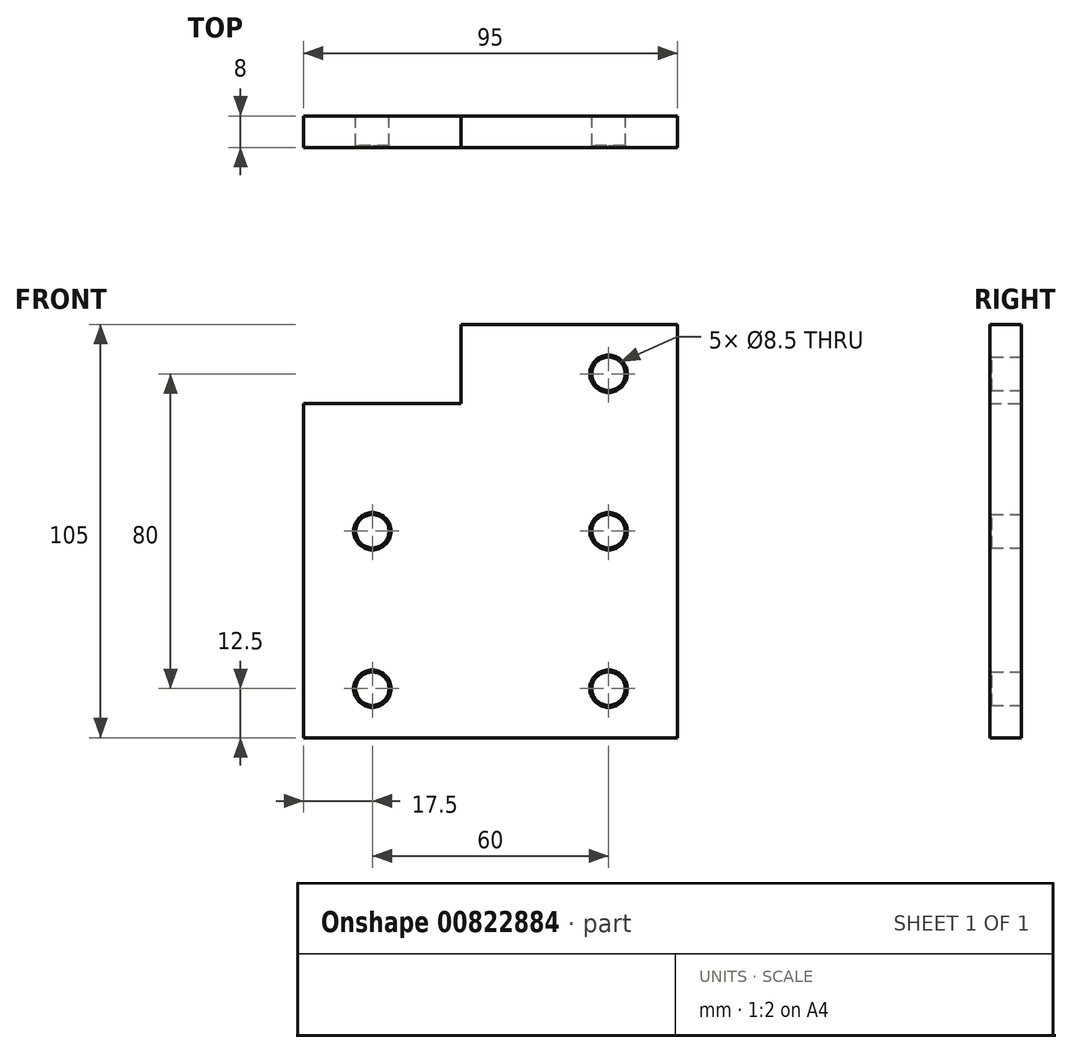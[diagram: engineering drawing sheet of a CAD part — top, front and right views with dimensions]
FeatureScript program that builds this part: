
annotation { "Feature Type Name" : "Feature", "Feature Type Description" : "" }
export const myFeature = defineFeature(function(context is Context, id is Id, definition is map)
    precondition{}
    {
        {
            var Q0;
            Q0=qCreatedBy(makeId("Front.planeOp"),FACE);
            var sketch = newSketch(context, id + "F0", { "sketchPlane" : qUnion([Q0])});
            skLineSegment(sketch, "E0.bottom", {"start": v(50, -52.5) * mm, "end": v(-45, -52.5) * mm});
            skLineSegment(sketch, "E0.top", {"start": v(50, 52.5) * mm, "end": v(-45, 52.5) * mm});
            skLineSegment(sketch, "E0.left", {"start": v(50, -52.5) * mm, "end": v(50, 52.5) * mm});
            skLineSegment(sketch, "E0.right", {"start": v(-45, -52.5) * mm, "end": v(-45, 52.5) * mm});
            skLineSegment(sketch, "E1", {"start": v(2.5, 0) * mm, "end": v(0, 0) * mm, "construction": true});
            skLineSegment(sketch, "E2.bottom", {"start": v(-27.5, 40) * mm, "end": v(32.5, 40) * mm, "construction": true});
            skLineSegment(sketch, "E2.top", {"start": v(-27.5, -40) * mm, "end": v(32.5, -40) * mm, "construction": true});
            skLineSegment(sketch, "E2.left", {"start": v(-27.5, 40) * mm, "end": v(-27.5, -40) * mm, "construction": true});
            skLineSegment(sketch, "E2.right", {"start": v(32.5, 40) * mm, "end": v(32.5, -40) * mm, "construction": true});
            skPoint(sketch, "E2.middle", {"position": v(2.5, 0) * mm});
            skCircle(sketch, "E3", {"center": v(-27.5, 40) * mm, "radius": 4.25 * mm, "construction": true});
            skCircle(sketch, "E4", {"center": v(32.5, 40) * mm, "radius": 4.25 * mm});
            skCircle(sketch, "E5", {"center": v(32.5, -40) * mm, "radius": 4.25 * mm});
            skCircle(sketch, "E6", {"center": v(-27.5, -40) * mm, "radius": 4.25 * mm});
            skCircle(sketch, "E7", {"center": v(-27.5, -40) * mm, "radius": 9 * mm, "construction": true});
            skLineSegment(sketch, "E8", {"start": v(-27.5, 0) * mm, "end": v(32.5, 0) * mm, "construction": true});
            skCircle(sketch, "E9", {"center": v(-27.5, 0) * mm, "radius": 4.25 * mm});
            skCircle(sketch, "E10", {"center": v(32.5, 0) * mm, "radius": 4.25 * mm});
            skSolve(sketch);
        }
        {
            var Q0;
            Q0=qSketchRegion(id+"F0",true);
            extrude(context, id + "F1", {"entities" : qUnion([Q0]), "depth" : 8 * mm, "offsetDistance" : 25 * mm});
        }
        {
            var Q0;
            Q0=makeQuery(id+"F1.opExtrude","CAP_EDGE",EDGE,{"disambiguationData":[OSD([sQuery(id+"F0.wireOp",EDGE,"E3")])],"isStart":false});
            var Q1;
            Q1=makeQuery(id+"F1.opExtrude","CAP_EDGE",EDGE,{"disambiguationData":[OSD([sQuery(id+"F0.wireOp",EDGE,"E4")])],"isStart":false});
            var Q2;
            Q2=makeQuery(id+"F1.opExtrude","CAP_EDGE",EDGE,{"disambiguationData":[OSD([sQuery(id+"F0.wireOp",EDGE,"E5")])],"isStart":false});
            var Q3;
            Q3=makeQuery(id+"F1.opExtrude","CAP_EDGE",EDGE,{"disambiguationData":[OSD([sQuery(id+"F0.wireOp",EDGE,"E6")])],"isStart":false});
            var Q4;
            Q4=makeQuery(id+"F1.opExtrude","CAP_EDGE",EDGE,{"disambiguationData":[OSD([sQuery(id+"F0.wireOp",EDGE,"E9")])],"isStart":false});
            var Q5;
            Q5=makeQuery(id+"F1.opExtrude","CAP_EDGE",EDGE,{"disambiguationData":[OSD([sQuery(id+"F0.wireOp",EDGE,"E10")])],"isStart":false});
            chamfer(context, id + "F2", {"entities" : qUnion([Q0, Q1, Q2, Q3, Q4, Q5]), "width" : 0.5 * mm, "tangentPropagation" : true});
        }
        {
            var Q0;
            Q0=makeQuery(id+"F1.opExtrude","CAP_FACE",FACE,{"disambiguationData":[OSD([sQuery(id+"F0.wireOp",EDGE,"E0.bottom"),sQuery(id+"F0.wireOp",EDGE,"E0.top"),sQuery(id+"F0.wireOp",EDGE,"E0.left"),sQuery(id+"F0.wireOp",EDGE,"E0.right"),sQuery(id+"F0.wireOp",EDGE,"E4"),sQuery(id+"F0.wireOp",EDGE,"E5"),sQuery(id+"F0.wireOp",EDGE,"E6"),sQuery(id+"F0.wireOp",EDGE,"E9"),sQuery(id+"F0.wireOp",EDGE,"E10")])],"isStart":false});
            var sketch = newSketch(context, id + "F3", { "sketchPlane" : qUnion([Q0])});
            skLineSegment(sketch, "E11.0", {"start": v(50, 52.5) * mm, "end": v(-45, 52.5) * mm, "construction": true});
            skLineSegment(sketch, "E12.0", {"start": v(-45, -52.5) * mm, "end": v(-45, 52.5) * mm, "construction": true});
            skLineSegment(sketch, "E13", {"start": v(-47.5, -14.2) * mm, "end": v(-47.5, 76.2) * mm, "construction": true});
            skLineSegment(sketch, "E14", {"start": v(-47.5, 76.2) * mm, "end": v(22.85, 76.2) * mm, "construction": true});
            skCircle(sketch, "E15", {"center": v(-17.5, 50.2) * mm, "radius": 12.5 * mm, "construction": true});
            skCircle(sketch, "E16", {"center": v(-17.5, 50.2) * mm, "radius": 10 * mm, "construction": true});
            skLineSegment(sketch, "E17", {"start": v(-5, 32.5) * mm, "end": v(-55, 32.5) * mm});
            skLineSegment(sketch, "E18", {"start": v(-55, 32.5) * mm, "end": v(-55, 88.36) * mm});
            skLineSegment(sketch, "E19", {"start": v(-5, 32.5) * mm, "end": v(-5, 88.36) * mm});
            skLineSegment(sketch, "E20", {"start": v(-5, 88.36) * mm, "end": v(-55, 88.36) * mm});
            skSolve(sketch);
        }
        {
            var Q0;
            Q0 = qSketchRegion(id + "F3", true);
            extrude(context, id + "F4", {"entities" : qUnion([Q0]), "operationType" : NewBodyOperationType.REMOVE, "oppositeDirection" : true, "depth" : 25 * mm, "offsetDistance" : 25 * mm});
        }
    });
